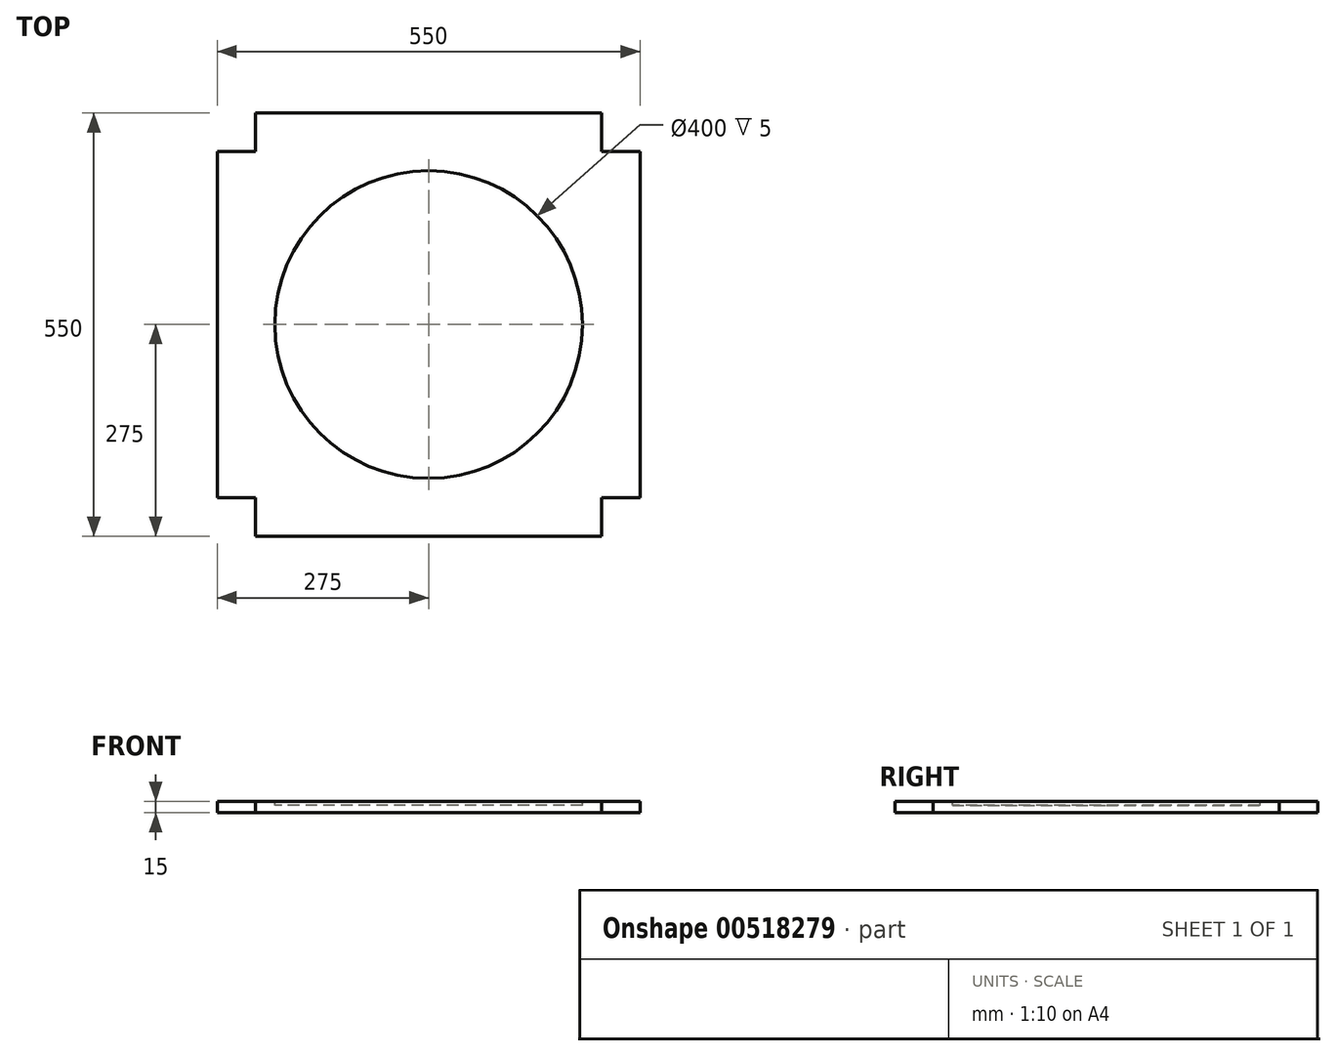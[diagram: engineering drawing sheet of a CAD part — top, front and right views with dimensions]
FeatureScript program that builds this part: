
annotation { "Feature Type Name" : "Feature", "Feature Type Description" : "" }
export const myFeature = defineFeature(function(context is Context, id is Id, definition is map)
    precondition{}
    {
        {
            var Q0;
            Q0=qCreatedBy(makeId("Top.planeOp"),FACE);
            var sketch = newSketch(context, id + "F0", { "sketchPlane" : qUnion([Q0])});
            skLineSegment(sketch, "E0.bottom", {"start": v(275, -275) * mm, "end": v(-275, -275) * mm});
            skLineSegment(sketch, "E0.top", {"start": v(275, 275) * mm, "end": v(-275, 275) * mm});
            skLineSegment(sketch, "E0.left", {"start": v(275, -275) * mm, "end": v(275, 275) * mm});
            skLineSegment(sketch, "E0.right", {"start": v(-275, -275) * mm, "end": v(-275, 275) * mm});
            skPoint(sketch, "E0.middle", {"position": v(0, 0) * mm});
            skSolve(sketch);
        }
        {
            var Q0;
            Q0 = qSketchRegion(id + "F0", true);
            extrude(context, id + "F1", {"entities" : qUnion([Q0]), "depth" : 15 * mm, "offsetDistance" : 25 * mm});
        }
        {
            var Q0;
            Q0=makeQuery(id+"F1.opExtrude","CAP_FACE",FACE,{"disambiguationData":[OSD([sQuery(id+"F0.wireOp",EDGE,"E0.bottom"),sQuery(id+"F0.wireOp",EDGE,"E0.top"),sQuery(id+"F0.wireOp",EDGE,"E0.left"),sQuery(id+"F0.wireOp",EDGE,"E0.right")])],"isStart":false});
            var sketch = newSketch(context, id + "F2", { "sketchPlane" : qUnion([Q0])});
            skCircle(sketch, "E1", {"center": v(0, 0) * mm, "radius": 200 * mm});
            skSolve(sketch);
        }
        {
            var Q0;
            Q0=qSketchRegion(id+"F2",true);
            extrude(context, id + "F3", {"entities" : qUnion([Q0]), "operationType" : NewBodyOperationType.REMOVE, "oppositeDirection" : true, "depth" : 5 * mm, "offsetDistance" : 25 * mm});
        }
        {
            var Q0;
            Q0=makeQuery(id+"F1.opExtrude","CAP_FACE",FACE,{"disambiguationData":[OSD([sQuery(id+"F0.wireOp",EDGE,"E0.bottom"),sQuery(id+"F0.wireOp",EDGE,"E0.top"),sQuery(id+"F0.wireOp",EDGE,"E0.left"),sQuery(id+"F0.wireOp",EDGE,"E0.right")])],"isStart":true});
            var sketch = newSketch(context, id + "F4", { "sketchPlane" : qUnion([Q0])});
            skLineSegment(sketch, "E2.bottom", {"start": v(-275, 275) * mm, "end": v(-225, 275) * mm});
            skLineSegment(sketch, "E2.top", {"start": v(-275, 225) * mm, "end": v(-225, 225) * mm});
            skLineSegment(sketch, "E2.left", {"start": v(-275, 275) * mm, "end": v(-275, 225) * mm});
            skLineSegment(sketch, "E2.right", {"start": v(-225, 275) * mm, "end": v(-225, 225) * mm});
            skLineSegment(sketch, "E3.MirrorCS", {"start": v(275, 275) * mm, "end": v(275, 225) * mm});
            skLineSegment(sketch, "E4.MirrorCS", {"start": v(275, 225) * mm, "end": v(225, 225) * mm});
            skLineSegment(sketch, "E5.MirrorCS", {"start": v(275, 275) * mm, "end": v(225, 275) * mm});
            skLineSegment(sketch, "E6.MirrorCS", {"start": v(225, 275) * mm, "end": v(225, 225) * mm});
            skLineSegment(sketch, "E7.MirrorCS", {"start": v(-275, -275) * mm, "end": v(-225, -275) * mm});
            skLineSegment(sketch, "E8.MirrorCS", {"start": v(-275, -275) * mm, "end": v(-275, -225) * mm});
            skLineSegment(sketch, "E9.MirrorCS", {"start": v(-225, -275) * mm, "end": v(-225, -225) * mm});
            skLineSegment(sketch, "E10.MirrorCS", {"start": v(-275, -225) * mm, "end": v(-225, -225) * mm});
            skLineSegment(sketch, "E11.MirrorCS", {"start": v(275, -275) * mm, "end": v(225, -275) * mm});
            skLineSegment(sketch, "E12.MirrorCS", {"start": v(275, -225) * mm, "end": v(225, -225) * mm});
            skLineSegment(sketch, "E13.MirrorCS", {"start": v(225, -275) * mm, "end": v(225, -225) * mm});
            skLineSegment(sketch, "E14.MirrorCS", {"start": v(275, -275) * mm, "end": v(275, -225) * mm});
            skSolve(sketch);
        }
        {
            var Q0;
            Q0 = qSketchRegion(id + "F4", true);
            extrude(context, id + "F5", {"entities" : qUnion([Q0]), "operationType" : NewBodyOperationType.REMOVE, "endBound" : BoundingType.UP_TO_NEXT, "oppositeDirection" : true, "depth" : 25 * mm, "offsetDistance" : 25 * mm});
        }
    });
